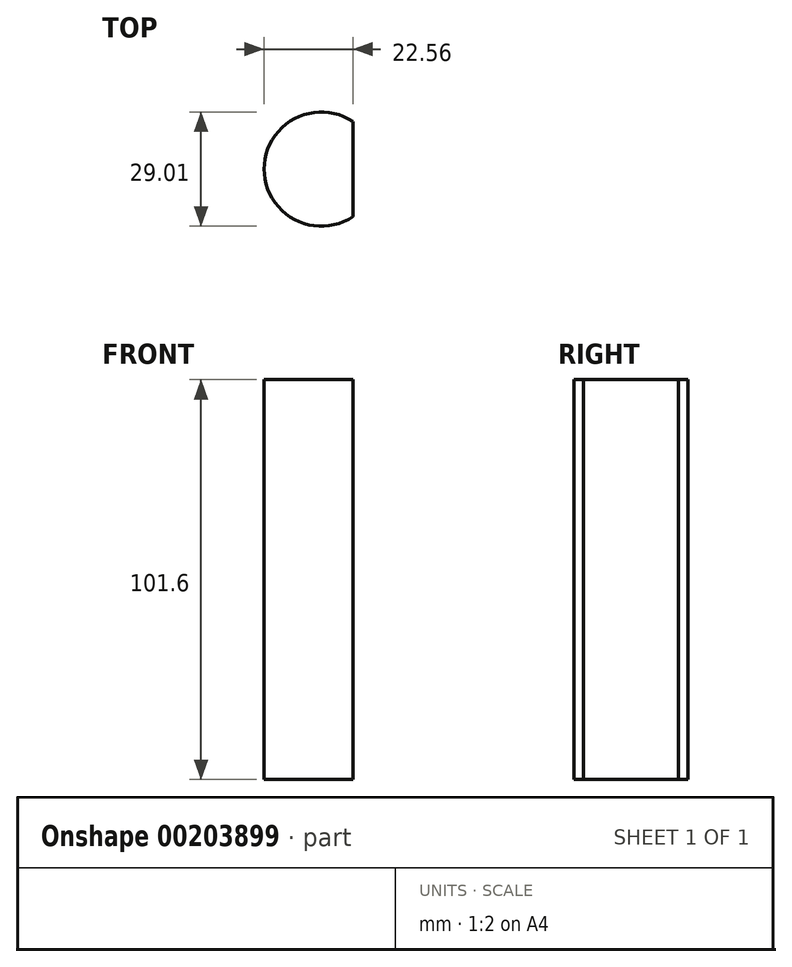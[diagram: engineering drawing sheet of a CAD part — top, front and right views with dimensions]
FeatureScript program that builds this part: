
annotation { "Feature Type Name" : "Feature", "Feature Type Description" : "" }
export const myFeature = defineFeature(function(context is Context, id is Id, definition is map)
    precondition{}
    {
        {
            var Q0;
            Q0=qCreatedBy(makeId("Top.planeOp"),FACE);
            var sketch = newSketch(context, id + "F0", { "sketchPlane" : qUnion([Q0])});
            skArc(sketch, "E0", {"start": v(-87.97, 43.1) * mm, "mid": v(-110.53, 31.03) * mm, "end": v(-87.97, 18.95) * mm});
            skLineSegment(sketch, "E1", {"start": v(-87.97, 43.1) * mm, "end": v(-87.97, 18.95) * mm});
            skSolve(sketch);
        }
        {
            var Q0;
            Q0=makeQuery(id+"F0.imprint","IMPRINT",FACE,{"disambiguationData":[TD([[makeQuery(id+"F0.imprint","IMPRINT",EDGE,{"derivedFrom":sQuery(id+"F0.wireOp",EDGE,"E0")}),1.0]])]});
            extrude(context, id + "F1", {"entities" : qUnion([Q0]), "depth" : 101.6 * mm});
        }
    });
